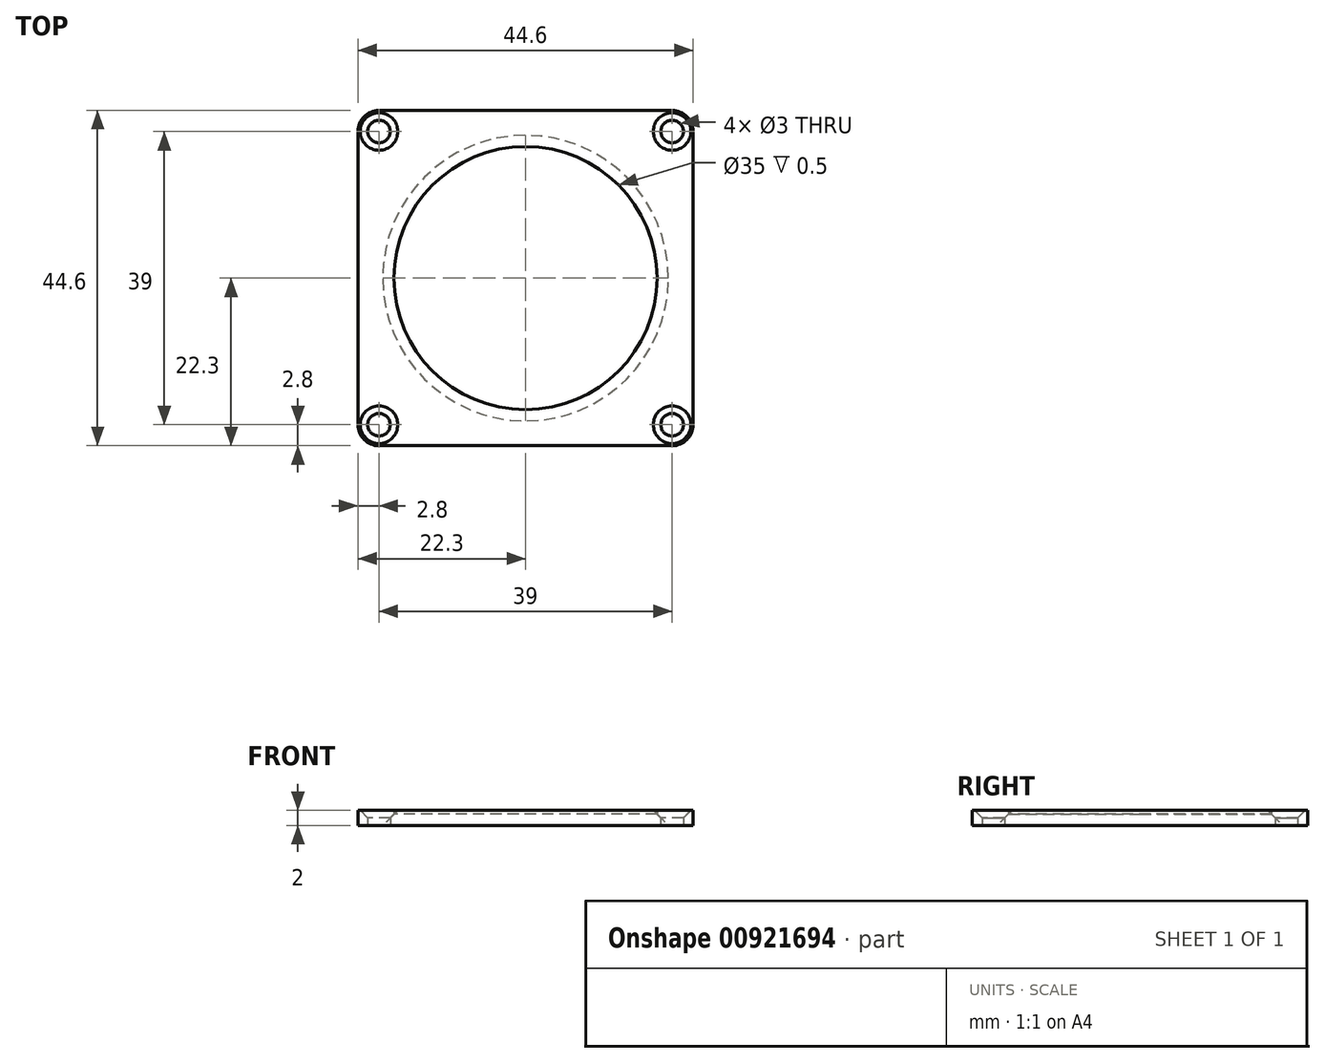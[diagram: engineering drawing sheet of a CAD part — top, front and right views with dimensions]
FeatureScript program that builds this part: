
annotation { "Feature Type Name" : "Feature", "Feature Type Description" : "" }
export const myFeature = defineFeature(function(context is Context, id is Id, definition is map)
    precondition{}
    {
        {
            var Q0;
            Q0=qCreatedBy(makeId("Top.planeOp"),FACE);
            var sketch = newSketch(context, id + "F0", { "sketchPlane" : qUnion([Q0])});
            skCircle(sketch, "E0", {"center": v(0, 0) * mm, "radius": 19 * mm});
            skArc(sketch, "E1.0", {"start": v(-22.3, -19.5) * mm, "mid": v(-21.48, -21.48) * mm, "end": v(-19.5, -22.3) * mm});
            skLineSegment(sketch, "E1.1", {"start": v(-19.5, -22.3) * mm, "end": v(19.5, -22.3) * mm});
            skLineSegment(sketch, "E1.2", {"start": v(-22.3, -19.5) * mm, "end": v(-22.3, 19.5) * mm});
            skArc(sketch, "E1.3", {"start": v(19.5, -22.3) * mm, "mid": v(21.48, -21.48) * mm, "end": v(22.3, -19.5) * mm});
            skArc(sketch, "E1.4", {"start": v(-19.5, 22.3) * mm, "mid": v(-21.48, 21.48) * mm, "end": v(-22.3, 19.5) * mm});
            skLineSegment(sketch, "E1.5", {"start": v(19.5, 22.3) * mm, "end": v(-19.5, 22.3) * mm});
            skArc(sketch, "E1.6", {"start": v(22.3, 19.5) * mm, "mid": v(21.48, 21.48) * mm, "end": v(19.5, 22.3) * mm});
            skLineSegment(sketch, "E1.7", {"start": v(22.3, -19.5) * mm, "end": v(22.3, 19.5) * mm});
            skCircle(sketch, "E2", {"center": v(-19.5, 19.5) * mm, "radius": 1.5 * mm});
            skCircle(sketch, "E3", {"center": v(19.5, 19.5) * mm, "radius": 1.5 * mm});
            skCircle(sketch, "E4", {"center": v(19.5, -19.5) * mm, "radius": 1.5 * mm});
            skCircle(sketch, "E5", {"center": v(-19.5, -19.5) * mm, "radius": 1.5 * mm});
            skCircle(sketch, "E6.0", {"center": v(0, 0) * mm, "radius": 17.5 * mm});
            skSolve(sketch);
        }
        {
            var Q0;
            Q0=makeQuery(id+"F0.imprint","IMPRINT",FACE,{"disambiguationData":[TD([[makeQuery(id+"F0.imprint","IMPRINT",EDGE,{"derivedFrom":sQuery(id+"F0.wireOp",EDGE,"E0")}),1.0]])]});
            var Q1;
            Q1=makeQuery(id+"F0.imprint","IMPRINT",FACE,{"disambiguationData":[TD([[makeQuery(id+"F0.imprint","IMPRINT",EDGE,{"derivedFrom":sQuery(id+"F0.wireOp",EDGE,"E0")}),-1.0]])]});
            extrude(context, id + "F1", {"entities" : qUnion([Q0, Q1]), "depth" : 2 * mm, "offsetDistance" : 25 * mm});
        }
        {
            var Q0;
            Q0=makeQuery(id+"F1.opExtrude","CAP_EDGE",EDGE,{"disambiguationData":[OSD([sQuery(id+"F0.wireOp",EDGE,"E2")])],"isStart":false});
            var Q1;
            Q1=makeQuery(id+"F1.opExtrude","CAP_EDGE",EDGE,{"disambiguationData":[OSD([sQuery(id+"F0.wireOp",EDGE,"E3")])],"isStart":false});
            var Q2;
            Q2=makeQuery(id+"F1.opExtrude","CAP_EDGE",EDGE,{"disambiguationData":[OSD([sQuery(id+"F0.wireOp",EDGE,"E4")])],"isStart":false});
            var Q3;
            Q3=makeQuery(id+"F1.opExtrude","CAP_EDGE",EDGE,{"disambiguationData":[OSD([sQuery(id+"F0.wireOp",EDGE,"E5")])],"isStart":false});
            chamfer(context, id + "F2", {"entities" : qUnion([Q0, Q1, Q2, Q3]), "width" : 1 * mm, "tangentPropagation" : true});
        }
        {
            var Q0;
            Q0=makeQuery(id+"F1.opExtrude","CAP_EDGE",EDGE,{"disambiguationData":[OSD([sQuery(id+"F0.wireOp",EDGE,"E6.0")])],"isStart":true});
            chamfer(context, id + "F3", {"entities" : qUnion([Q0]), "width" : 1.5 * mm, "tangentPropagation" : true});
        }
    });
